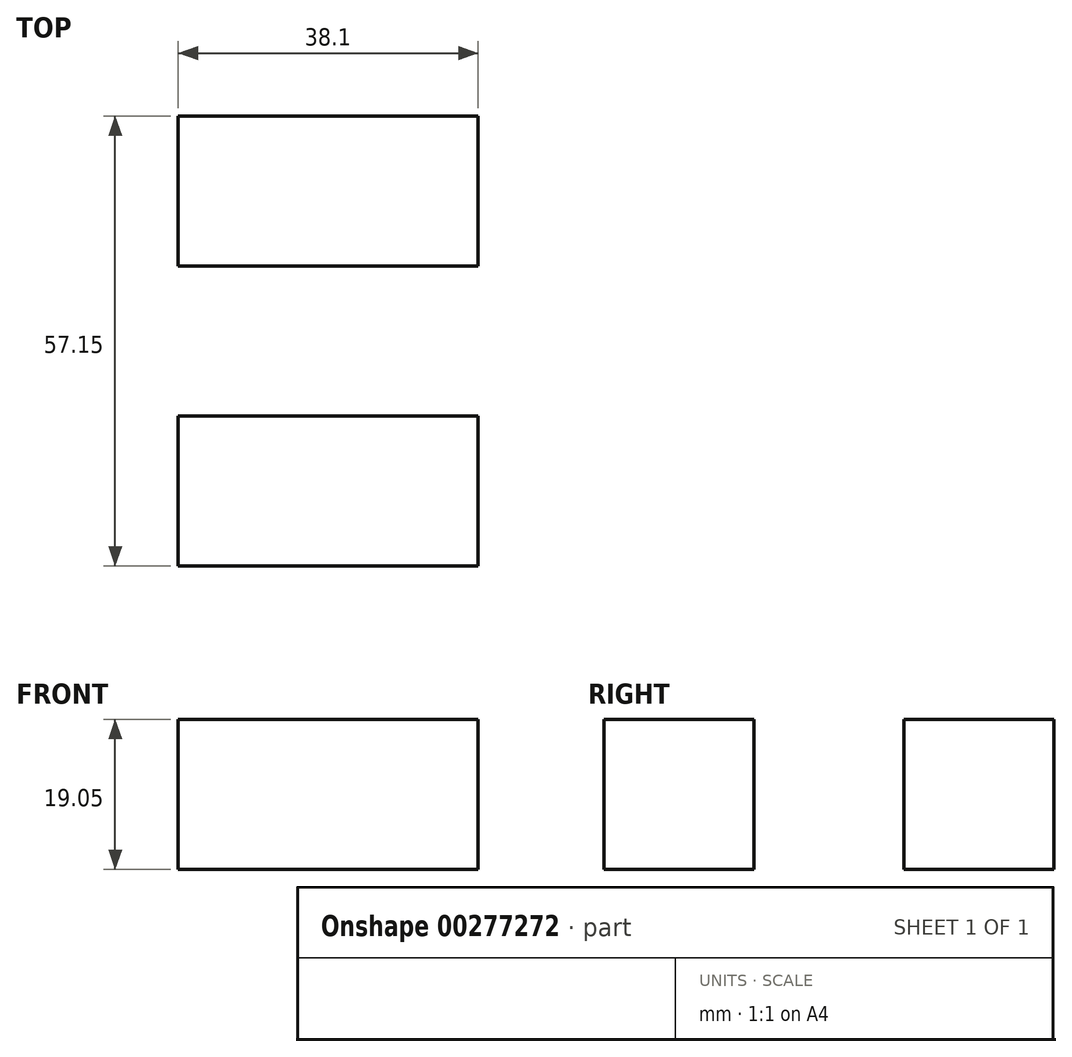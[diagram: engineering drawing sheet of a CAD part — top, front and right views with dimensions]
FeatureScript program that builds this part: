
annotation { "Feature Type Name" : "Feature", "Feature Type Description" : "" }
export const myFeature = defineFeature(function(context is Context, id is Id, definition is map)
    precondition{}
    {
        {
            var Q0;
            Q0=qCreatedBy(makeId("Top.planeOp"),FACE);
            var sketch = newSketch(context, id + "F0", { "sketchPlane" : qUnion([Q0])});
            skLineSegment(sketch, "E0.bottom", {"start": v(19.05, 32.68) * mm, "end": v(0, 32.68) * mm});
            skLineSegment(sketch, "E0.top", {"start": v(19.05, 51.73) * mm, "end": v(0, 51.73) * mm});
            skLineSegment(sketch, "E0.left", {"start": v(19.05, 32.68) * mm, "end": v(19.05, 51.73) * mm});
            skLineSegment(sketch, "E0.right", {"start": v(0, 32.68) * mm, "end": v(0, 51.73) * mm});
            skLineSegment(sketch, "E1.bottom", {"start": v(0, 51.73) * mm, "end": v(-19.05, 51.73) * mm});
            skLineSegment(sketch, "E1.top", {"start": v(0, 32.68) * mm, "end": v(-19.05, 32.68) * mm});
            skLineSegment(sketch, "E1.left", {"start": v(0, 51.73) * mm, "end": v(0, 32.68) * mm});
            skLineSegment(sketch, "E1.right", {"start": v(-19.05, 51.73) * mm, "end": v(-19.05, 32.68) * mm});
            skLineSegment(sketch, "E2.bottom", {"start": v(-19.05, 32.68) * mm, "end": v(0, 32.68) * mm});
            skLineSegment(sketch, "E2.top", {"start": v(-19.05, 13.63) * mm, "end": v(0, 13.63) * mm});
            skLineSegment(sketch, "E2.left", {"start": v(-19.05, 32.68) * mm, "end": v(-19.05, 13.63) * mm});
            skLineSegment(sketch, "E2.right", {"start": v(0, 32.68) * mm, "end": v(0, 13.63) * mm});
            skLineSegment(sketch, "E3.top", {"start": v(-19.05, -5.42) * mm, "end": v(0, -5.42) * mm});
            skLineSegment(sketch, "E3.left", {"start": v(-19.05, 13.63) * mm, "end": v(-19.05, -5.42) * mm});
            skLineSegment(sketch, "E3.right", {"start": v(0, 13.63) * mm, "end": v(0, -5.42) * mm});
            skLineSegment(sketch, "E4.bottom", {"start": v(0, 13.63) * mm, "end": v(19.05, 13.63) * mm});
            skLineSegment(sketch, "E4.top", {"start": v(0, -5.42) * mm, "end": v(19.05, -5.42) * mm});
            skLineSegment(sketch, "E4.right", {"start": v(19.05, 13.63) * mm, "end": v(19.05, -5.42) * mm});
            skSolve(sketch);
        }
        {
            var Q0;
            Q0=makeQuery(id+"F0.imprint","IMPRINT",FACE,{"disambiguationData":[TD([[makeQuery(id+"F0.imprint","IMPRINT",EDGE,{"derivedFrom":sQuery(id+"F0.wireOp",EDGE,"E1.bottom")}),1.0]])]});
            var Q1;
            Q1=makeQuery(id+"F0.imprint","IMPRINT",FACE,{"disambiguationData":[TD([[makeQuery(id+"F0.imprint","IMPRINT",EDGE,{"derivedFrom":sQuery(id+"F0.wireOp",EDGE,"E0.bottom")}),-1.0]])]});
            var Q2;
            Q2=makeQuery(id+"F0.imprint","IMPRINT",FACE,{"disambiguationData":[TD([[makeQuery(id+"F0.imprint","IMPRINT",EDGE,{"derivedFrom":sQuery(id+"F0.wireOp",EDGE,"E2.bottom")}),-1.0]])]});
            var Q3;
            Q3=makeQuery(id+"F0.imprint","IMPRINT",FACE,{"disambiguationData":[TD([[makeQuery(id+"F0.imprint","IMPRINT",EDGE,{"derivedFrom":sQuery(id+"F0.wireOp",EDGE,"E2.top")}),-1.0]])]});
            var Q4;
            Q4=makeQuery(id+"F0.imprint","IMPRINT",FACE,{"disambiguationData":[TD([[makeQuery(id+"F0.imprint","IMPRINT",EDGE,{"derivedFrom":sQuery(id+"F0.wireOp",EDGE,"E4.bottom")}),-1.0]])]});
            extrude(context, id + "F1", {"entities" : qUnion([Q0, Q1, Q2, Q3, Q4]), "depth" : 19.05 * mm});
        }
    });
